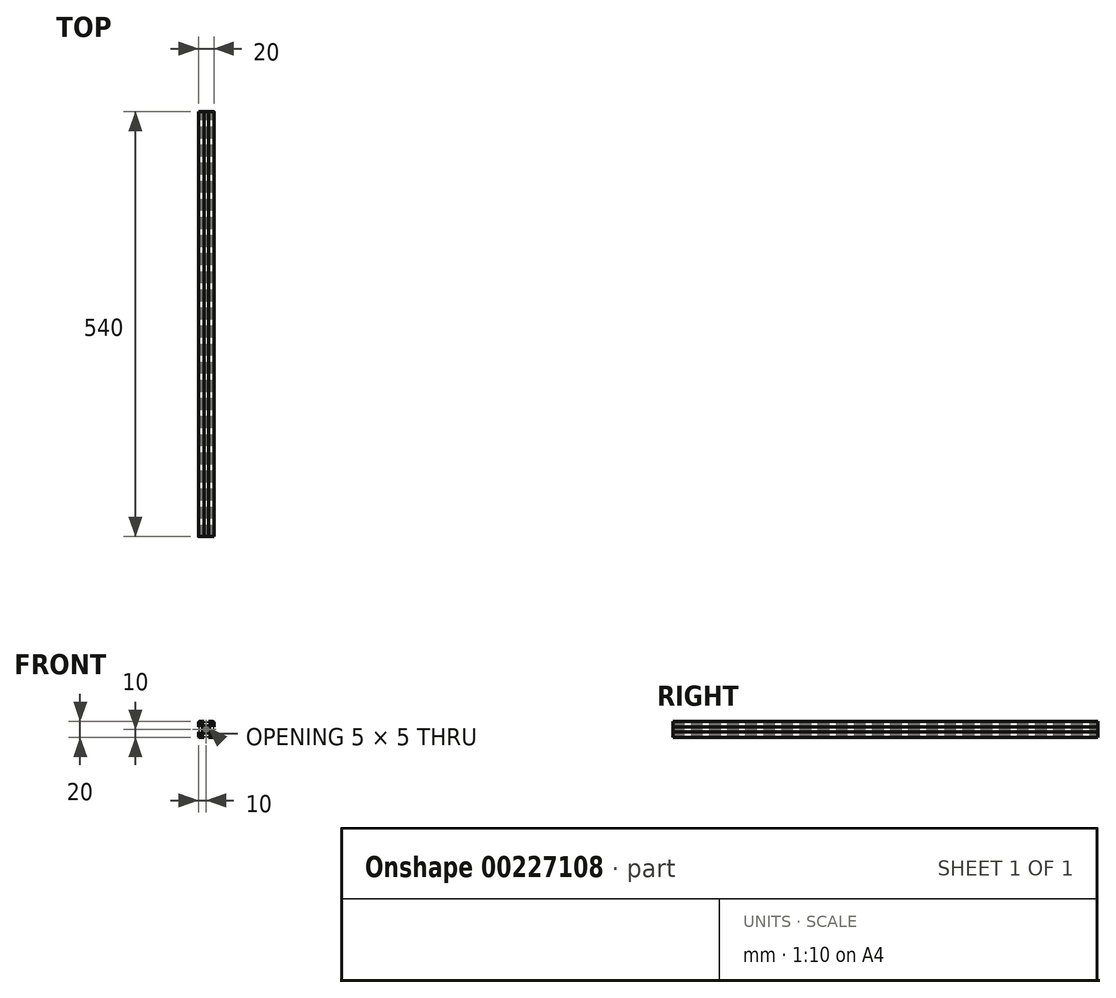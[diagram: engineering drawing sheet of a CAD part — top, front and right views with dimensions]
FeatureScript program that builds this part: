
annotation { "Feature Type Name" : "Feature", "Feature Type Description" : "" }
export const myFeature = defineFeature(function(context is Context, id is Id, definition is map)
    precondition{}
    {
        {
            var Q0;
            Q0=qCreatedBy(makeId("Front.planeOp"),FACE);
            var sketch = newSketch(context, id + "F0", { "sketchPlane" : qUnion([Q0])});
            skLineSegment(sketch, "E0.bottom", {"start": v(8.5, -10) * mm, "end": v(3, -10) * mm});
            skLineSegment(sketch, "E0.top", {"start": v(8.5, 10) * mm, "end": v(3, 10) * mm});
            skLineSegment(sketch, "E0.left", {"start": v(10, -8.5) * mm, "end": v(10, -3) * mm});
            skLineSegment(sketch, "E0.right", {"start": v(-10, -8.5) * mm, "end": v(-10, -3) * mm});
            skPoint(sketch, "E0.middle", {"position": v(0, 0) * mm});
            skLineSegment(sketch, "E1.bottom", {"start": v(6, -8.5) * mm, "end": v(3, -8.5) * mm});
            skLineSegment(sketch, "E1.top", {"start": v(6, 8.5) * mm, "end": v(3, 8.5) * mm});
            skLineSegment(sketch, "E1.left", {"start": v(8.5, -6) * mm, "end": v(8.5, -3) * mm});
            skLineSegment(sketch, "E1.right", {"start": v(-8.5, -6) * mm, "end": v(-8.5, -3) * mm});
            skLineSegment(sketch, "E2.bottom", {"start": v(3.44, -4.5) * mm, "end": v(-3.44, -4.5) * mm});
            skLineSegment(sketch, "E2.top", {"start": v(3.44, 4.5) * mm, "end": v(-3.44, 4.5) * mm});
            skLineSegment(sketch, "E2.left", {"start": v(4.5, -3.44) * mm, "end": v(4.5, 3.44) * mm});
            skLineSegment(sketch, "E2.right", {"start": v(-4.5, -3.44) * mm, "end": v(-4.5, 3.44) * mm});
            skLineSegment(sketch, "E3.bottom", {"start": v(8.5, -6) * mm, "end": v(7.06, -6) * mm});
            skLineSegment(sketch, "E3.top", {"start": v(8.5, 6) * mm, "end": v(7.06, 6) * mm});
            skLineSegment(sketch, "E4.left", {"start": v(6, -8.5) * mm, "end": v(6, -7.06) * mm});
            skLineSegment(sketch, "E4.right", {"start": v(-6, -8.5) * mm, "end": v(-6, -7.06) * mm});
            skPoint(sketch, "E5.orphan", {"position": v(-8.5, 8.5) * mm});
            skPoint(sketch, "E6.orphan", {"position": v(8.5, 8.5) * mm});
            skPoint(sketch, "E7.orphan", {"position": v(8.5, -8.5) * mm});
            skPoint(sketch, "E8.orphan", {"position": v(-8.5, -8.5) * mm});
            skLineSegment(sketch, "E9.trimOffspring", {"start": v(-6, 7.06) * mm, "end": v(-6, 8.5) * mm});
            skLineSegment(sketch, "E10.trimOffspring", {"start": v(-7.06, 6) * mm, "end": v(-8.5, 6) * mm});
            skLineSegment(sketch, "E11.trimOffspring", {"start": v(6, 7.06) * mm, "end": v(6, 8.5) * mm});
            skLineSegment(sketch, "E12.trimOffspring", {"start": v(-7.06, -6) * mm, "end": v(-8.5, -6) * mm});
            skLineSegment(sketch, "E13", {"start": v(-10, 10) * mm, "end": v(0, 0) * mm, "construction": true});
            skLineSegment(sketch, "E14", {"start": v(10, 10) * mm, "end": v(0, 0) * mm, "construction": true});
            skLineSegment(sketch, "E15", {"start": v(-6, 7.06) * mm, "end": v(-3.44, 4.5) * mm});
            skPoint(sketch, "E15.endSnap0", {"position": v(7.25, -6) * mm});
            skLineSegment(sketch, "E16", {"start": v(6, -7.06) * mm, "end": v(3.44, -4.5) * mm});
            skLineSegment(sketch, "E17", {"start": v(7.06, 6) * mm, "end": v(4.5, 3.44) * mm});
            skLineSegment(sketch, "E18", {"start": v(6, 7.06) * mm, "end": v(3.44, 4.5) * mm});
            skPoint(sketch, "E19.orphan", {"position": v(6, -6) * mm});
            skPoint(sketch, "E20.orphan", {"position": v(-4.5, -4.5) * mm});
            skPoint(sketch, "E21.orphan", {"position": v(-4.5, 4.5) * mm});
            skPoint(sketch, "E22.orphan", {"position": v(4.5, 4.5) * mm});
            skPoint(sketch, "E23.orphan", {"position": v(4.5, -4.5) * mm});
            skLineSegment(sketch, "E24.trimOffspring", {"start": v(4.5, -3.44) * mm, "end": v(7.06, -6) * mm});
            skLineSegment(sketch, "E25.trimOffspring", {"start": v(-3.44, -4.5) * mm, "end": v(-6, -7.06) * mm});
            skLineSegment(sketch, "E26.trimOffspring", {"start": v(-4.5, -3.44) * mm, "end": v(-7.06, -6) * mm});
            skLineSegment(sketch, "E27.trimOffspring", {"start": v(-4.5, 3.44) * mm, "end": v(-7.06, 6) * mm});
            skLineSegment(sketch, "E28.bottom", {"start": v(8.5, -3) * mm, "end": v(10, -3) * mm});
            skLineSegment(sketch, "E28.top", {"start": v(8.5, 3) * mm, "end": v(10, 3) * mm});
            skPoint(sketch, "E28.middle", {"position": v(10, 0) * mm});
            skLineSegment(sketch, "E29.left", {"start": v(3, 8.5) * mm, "end": v(3, 10) * mm});
            skLineSegment(sketch, "E29.right", {"start": v(-3, 8.5) * mm, "end": v(-3, 10) * mm});
            skPoint(sketch, "E29.middle", {"position": v(0, 10) * mm});
            skLineSegment(sketch, "E30.bottom", {"start": v(-8.5, 3) * mm, "end": v(-10, 3) * mm});
            skLineSegment(sketch, "E30.top", {"start": v(-8.5, -3) * mm, "end": v(-10, -3) * mm});
            skPoint(sketch, "E30.middle", {"position": v(-10, 0) * mm});
            skLineSegment(sketch, "E31.left", {"start": v(3, -8.5) * mm, "end": v(3, -10) * mm});
            skLineSegment(sketch, "E31.right", {"start": v(-3, -8.5) * mm, "end": v(-3, -10) * mm});
            skPoint(sketch, "E31.middle", {"position": v(0, -10) * mm});
            skPoint(sketch, "E32.orphan", {"position": v(3, 11.5) * mm});
            skPoint(sketch, "E33.orphan", {"position": v(-3, 11.5) * mm});
            skLineSegment(sketch, "E34.trimOffspring", {"start": v(-3, 10) * mm, "end": v(-8.5, 10) * mm});
            skLineSegment(sketch, "E35.trimOffspring", {"start": v(-3, 8.5) * mm, "end": v(-6, 8.5) * mm});
            skPoint(sketch, "E28.right.end.orphan", {"position": v(11.5, 3) * mm});
            skPoint(sketch, "E36.orphan", {"position": v(11.5, -3) * mm});
            skLineSegment(sketch, "E37.trimOffspring", {"start": v(10, 3) * mm, "end": v(10, 8.5) * mm});
            skLineSegment(sketch, "E38.trimOffspring", {"start": v(8.5, 3) * mm, "end": v(8.5, 6) * mm});
            skPoint(sketch, "E39.orphan", {"position": v(3, -11.5) * mm});
            skPoint(sketch, "E40.orphan", {"position": v(-3, -11.5) * mm});
            skLineSegment(sketch, "E41.trimOffspring", {"start": v(-3, -10) * mm, "end": v(-8.5, -10) * mm});
            skLineSegment(sketch, "E42.trimOffspring", {"start": v(-3, -8.5) * mm, "end": v(-6, -8.5) * mm});
            skPoint(sketch, "E30.right.end.orphan", {"position": v(-11.5, -3) * mm});
            skPoint(sketch, "E43.orphan", {"position": v(-11.5, 3) * mm});
            skLineSegment(sketch, "E44.trimOffspring", {"start": v(-10, 3) * mm, "end": v(-10, 8.5) * mm});
            skLineSegment(sketch, "E45.trimOffspring", {"start": v(-8.5, 3) * mm, "end": v(-8.5, 6) * mm});
            skLineSegment(sketch, "E46.trimOffspring", {"start": v(0, 0) * mm, "end": v(10, -10) * mm, "construction": true});
            skLineSegment(sketch, "E47.trimOffspring", {"start": v(0, 0) * mm, "end": v(-10, -10) * mm, "construction": true});
            skArc(sketch, "E48", {"start": v(1.16, 2.22) * mm, "mid": v(0, 2.5) * mm, "end": v(-1.16, 2.22) * mm});
            skLineSegment(sketch, "E49", {"start": v(-2.5, -1.44) * mm, "end": v(1.44, 2.5) * mm});
            skLineSegment(sketch, "E50", {"start": v(2.5, 1.44) * mm, "end": v(-1.44, -2.5) * mm});
            skLineSegment(sketch, "E51", {"start": v(1.44, -2.5) * mm, "end": v(-2.5, 1.44) * mm});
            skLineSegment(sketch, "E52", {"start": v(-1.44, 2.5) * mm, "end": v(2.5, -1.44) * mm});
            skLineSegment(sketch, "E53", {"start": v(2.5, 1.44) * mm, "end": v(2.5, -1.44) * mm, "construction": true});
            skLineSegment(sketch, "E54", {"start": v(1.44, -2.5) * mm, "end": v(-1.44, -2.5) * mm, "construction": true});
            skLineSegment(sketch, "E55", {"start": v(-2.5, -1.44) * mm, "end": v(-2.5, 1.44) * mm, "construction": true});
            skLineSegment(sketch, "E56", {"start": v(-1.44, 2.5) * mm, "end": v(1.44, 2.5) * mm, "construction": true});
            skLineSegment(sketch, "E57", {"start": v(-1.44, 2.5) * mm, "end": v(-2.5, 1.44) * mm});
            skLineSegment(sketch, "E58", {"start": v(1.44, 2.5) * mm, "end": v(2.5, 1.44) * mm});
            skLineSegment(sketch, "E59", {"start": v(2.5, -1.44) * mm, "end": v(1.44, -2.5) * mm});
            skLineSegment(sketch, "E60", {"start": v(-1.44, -2.5) * mm, "end": v(-2.5, -1.44) * mm});
            skArc(sketch, "E61.trimOffspring", {"start": v(-2.22, 1.16) * mm, "mid": v(-2.5, 0) * mm, "end": v(-2.22, -1.16) * mm});
            skArc(sketch, "E62.trimOffspring", {"start": v(-1.16, -2.22) * mm, "mid": v(0, -2.5) * mm, "end": v(1.16, -2.22) * mm});
            skArc(sketch, "E63.trimOffspring", {"start": v(2.22, -1.16) * mm, "mid": v(2.5, 0) * mm, "end": v(2.22, 1.16) * mm});
            skPoint(sketch, "E64.visualSharp", {"position": v(10, 10) * mm});
            skArc(sketch, "E64.filletArc", {"start": v(10, 8.5) * mm, "mid": v(9.56, 9.56) * mm, "end": v(8.5, 10) * mm});
            skPoint(sketch, "E65.visualSharp", {"position": v(10, -10) * mm});
            skArc(sketch, "E65.filletArc", {"start": v(8.5, -10) * mm, "mid": v(9.56, -9.56) * mm, "end": v(10, -8.5) * mm});
            skPoint(sketch, "E66.visualSharp", {"position": v(-10, -10) * mm});
            skArc(sketch, "E66.filletArc", {"start": v(-10, -8.5) * mm, "mid": v(-9.56, -9.56) * mm, "end": v(-8.5, -10) * mm});
            skPoint(sketch, "E67.visualSharp", {"position": v(-10, 10) * mm});
            skArc(sketch, "E67.filletArc", {"start": v(-8.5, 10) * mm, "mid": v(-9.56, 9.56) * mm, "end": v(-10, 8.5) * mm});
            skSolve(sketch);
        }
        {
            assignVariable(context, id + "F2", {"name" : "Length", "anyValue" : 540});
        }
        {
            var Q0;
            Q0=qSketchRegion(id+"F0",true);
            extrude(context, id + "F1", {"entities" : qUnion([Q0]), "depth" : (getVariable(context, 'Length')) * mm});
        }
    });
